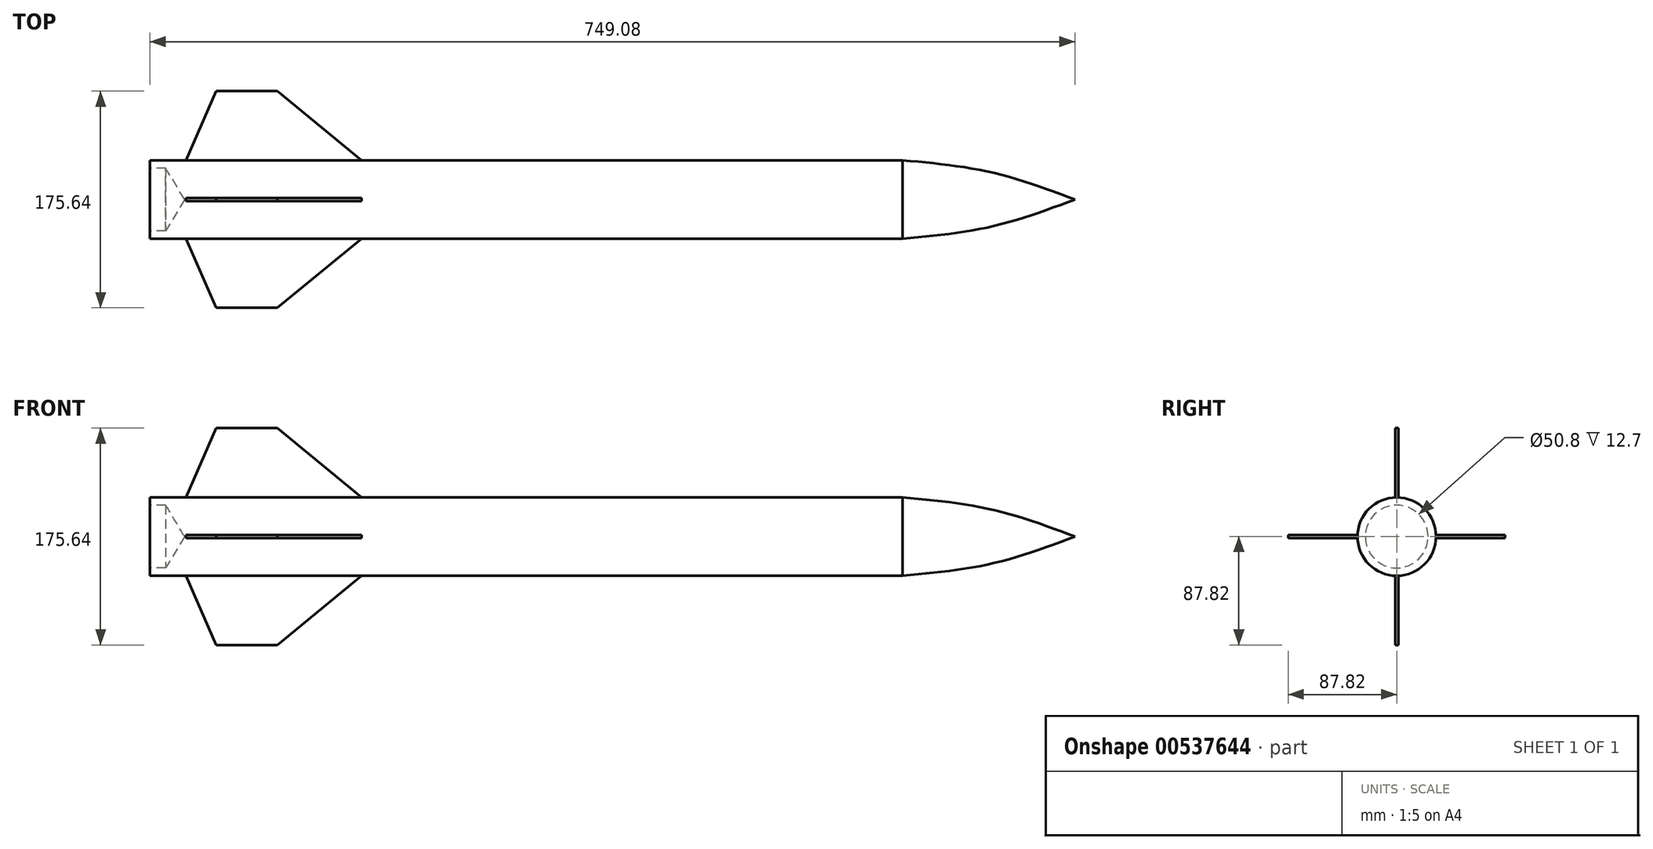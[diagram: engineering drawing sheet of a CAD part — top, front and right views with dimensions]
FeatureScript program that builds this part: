
annotation { "Feature Type Name" : "Feature", "Feature Type Description" : "" }
export const myFeature = defineFeature(function(context is Context, id is Id, definition is map)
    precondition{}
    {
        {
            var Q0;
            Q0=qCreatedBy(makeId("Front.planeOp"),FACE);
            var sketch = newSketch(context, id + "F0", { "sketchPlane" : qUnion([Q0])});
            skLineSegment(sketch, "E0.bottom", {"start": v(-304.8, 31.75) * mm, "end": v(304.8, 31.75) * mm});
            skLineSegment(sketch, "E0.top", {"start": v(-304.8, -31.75) * mm, "end": v(304.8, -31.75) * mm});
            skLineSegment(sketch, "E0.left", {"start": v(-304.8, 31.75) * mm, "end": v(-304.8, -31.75) * mm});
            skLineSegment(sketch, "E0.right", {"start": v(304.8, 31.75) * mm, "end": v(304.8, -31.75) * mm});
            skPoint(sketch, "E0.middle", {"position": v(0, 0) * mm});
            skLineSegment(sketch, "E1", {"start": v(-275.7, 31.75) * mm, "end": v(-251.24, 87.82) * mm});
            skLineSegment(sketch, "E2", {"start": v(-251.24, 87.82) * mm, "end": v(-201.81, 87.82) * mm});
            skLineSegment(sketch, "E3", {"start": v(-201.81, 87.82) * mm, "end": v(-133.4, 31.75) * mm});
            skFitSpline(sketch, "E4", {"points": [v(304.8, 31.75) * mm, v(376.87, 21.9) * mm, v(444.28, 0) * mm], "startDerivative": vector(145.1, -13.38) * mm, "endDerivative": vector(133.82, -50.2) * mm});
            skLineSegment(sketch, "E5", {"start": v(444.28, 0) * mm, "end": v(304.8, 0) * mm});
            skLineSegment(sketch, "E6", {"start": v(-304.8, 0) * mm, "end": v(304.8, 0) * mm});
            skLineSegment(sketch, "E7", {"start": v(-275.7, 31.75) * mm, "end": v(-133.4, 31.75) * mm});
            skSolve(sketch);
        }
        {
            var Q0;
            {var subQ0=sQuery(id+"F0.wireOp",EDGE,"E4");Q0=makeQuery(id+"F0.imprint","IMPRINT",FACE,{"disambiguationData":[TD([[makeQuery(id+"F0.imprint","IMPRINT",EDGE,{"derivedFrom":subQ0}),-1.0]])]});}
            var Q1;
            Q1=sQuery(id+"F0.wireOp",EDGE,"E5");
            revolve(context, id + "F1", {"entities" : qUnion([Q0]), "axis" : qUnion([Q1]), "revolveType" : RevolveType.FULL});
        }
        {
            var Q0;
            {var subQ6=sQuery(id+"F0.wireOp",EDGE,"E6");Q0=makeQuery(id+"F0.imprint","IMPRINT",FACE,{"disambiguationData":[TD([[makeQuery(id+"F0.imprint","IMPRINT",EDGE,{"derivedFrom":subQ6}),1.0]])]});}
            var Q1;
            Q1=sQuery(id+"F0.wireOp",EDGE,"E6");
            revolve(context, id + "F2", {"operationType" : NewBodyOperationType.ADD, "entities" : qUnion([Q0]), "axis" : qUnion([Q1]), "revolveType" : RevolveType.FULL});
        }
        {
            var Q0;
            Q0=makeQuery(id+"F0.imprint","IMPRINT",FACE,{"disambiguationData":[TD([[makeQuery(id+"F0.imprint","IMPRINT",EDGE,{"derivedFrom":sQuery(id+"F0.wireOp",EDGE,"E1")}),-1.0]])]});
            extrude(context, id + "F3", {"entities" : qUnion([Q0]), "operationType" : NewBodyOperationType.ADD, "endBound" : BoundingType.SYMMETRIC, "depth" : 2.54 * mm, "offsetDistance" : 25.4 * mm});
        }
        {
            var Q0;
            Q0=makeQuery(id+"F3.opExtrude","SWEPT_BODY",BODY,{"disambiguationData":[OSD([sQuery(id+"F0.wireOp",EDGE,"E1"),sQuery(id+"F0.wireOp",EDGE,"E2"),sQuery(id+"F0.wireOp",EDGE,"E3"),sQuery(id+"F0.wireOp",EDGE,"E7")])]});
            var Q1;
            Q1=sQuery(id+"F0.wireOp",EDGE,"E6");
            circularPattern(context, id + "F4", {"entities" : qUnion([Q0]), "axis" : qUnion([Q1]), "angle" : 360 * degree, "instanceCount" : 4, "equalSpace" : true});
        }
        {
            var Q0;
            Q0=makeQuery(id+"F2.opRevolve","SWEPT_FACE",FACE,{"disambiguationData":[OSD([sQuery(id+"F0.wireOp",EDGE,"E0.left")])]});
            var sketch = newSketch(context, id + "F5", { "sketchPlane" : qUnion([Q0])});
            skCircle(sketch, "E8", {"center": v(0, 0) * mm, "radius": 26.35 * mm});
            skSolve(sketch);
        }
        {
            var Q0;
            Q0=sQuery(id+"F5.wireOp",VERTEX,"E8.center");
            var Q1;
            Q1=makeQuery(id+"F1.opRevolve","SWEPT_BODY",BODY,{"disambiguationData":[OSD([sQuery(id+"F0.wireOp",EDGE,"E0.right"),sQuery(id+"F0.wireOp",EDGE,"E4"),sQuery(id+"F0.wireOp",EDGE,"E5")])]});
            hole(context, id + "F6", {"style" : HoleStyle.SIMPLE, "endStyle" : HoleEndStyle.BLIND, "holeDiameter" : 50.8 * mm, "holeDepth" : 12.7 * mm, "isTappedThrough" : true, "tappedDepth" : 12.7 * mm, "tapClearance" : 3, "locations" : qUnion([Q0]), "scope" : qUnion([Q1])});
        }
    });
